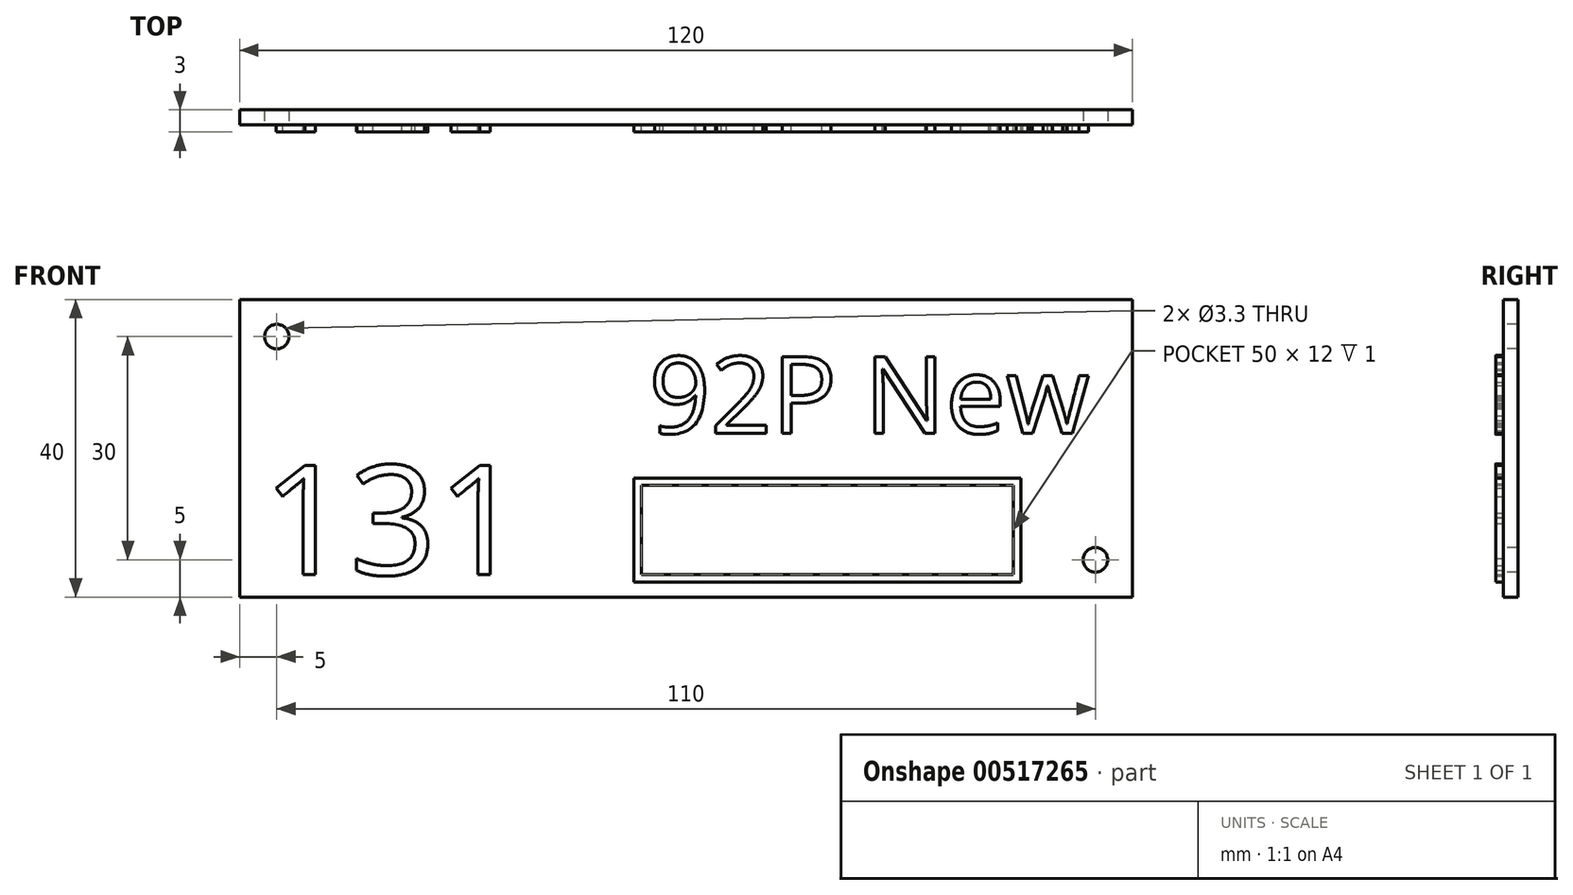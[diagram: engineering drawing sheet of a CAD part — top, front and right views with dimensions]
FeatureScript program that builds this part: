
annotation { "Feature Type Name" : "Feature", "Feature Type Description" : "" }
export const myFeature = defineFeature(function(context is Context, id is Id, definition is map)
    precondition{}
    {
        {
            var Q0;
            Q0=qCreatedBy(makeId("Front.planeOp"),FACE);
            var sketch = newSketch(context, id + "F0", { "sketchPlane" : qUnion([Q0])});
            skLineSegment(sketch, "E0.bottom", {"start": v(60, -20) * mm, "end": v(-60, -20) * mm});
            skLineSegment(sketch, "E0.top", {"start": v(60, 20) * mm, "end": v(-60, 20) * mm});
            skLineSegment(sketch, "E0.left", {"start": v(60, -20) * mm, "end": v(60, 20) * mm});
            skLineSegment(sketch, "E0.right", {"start": v(-60, -20) * mm, "end": v(-60, 20) * mm});
            skPoint(sketch, "E0.middle", {"position": v(0, 0) * mm});
            skSolve(sketch);
        }
        {
            var Q0;
            Q0=makeQuery(id+"F0.imprint","IMPRINT",FACE,{"disambiguationData":[TD([[makeQuery(id+"F0.imprint","IMPRINT",EDGE,{"derivedFrom":sQuery(id+"F0.wireOp",EDGE,"E0.bottom")}),-1.0]])]});
            extrude(context, id + "F1", {"entities" : qUnion([Q0]), "depth" : 2 * mm});
        }
        {
            var Q0;
            Q0=makeQuery(id+"F1.opExtrude","CAP_FACE",FACE,{"disambiguationData":[OSD([sQuery(id+"F0.wireOp",EDGE,"E0.bottom"),sQuery(id+"F0.wireOp",EDGE,"E0.top"),sQuery(id+"F0.wireOp",EDGE,"E0.left"),sQuery(id+"F0.wireOp",EDGE,"E0.right")])],"isStart":false});
            var sketch = newSketch(context, id + "F2", { "sketchPlane" : qUnion([Q0])});
            skPoint(sketch, "E1", {"position": v(-55, 15) * mm});
            skPoint(sketch, "E2", {"position": v(55, -15) * mm});
            skSolve(sketch);
        }
        {
            var Q0;
            Q0=sQuery(id+"F2.wireOp",VERTEX,"E1");
            var Q1;
            Q1=sQuery(id+"F2.wireOp",VERTEX,"E2");
            var Q2;
            Q2=makeQuery(id+"F1.opExtrude","SWEPT_BODY",BODY,{"disambiguationData":[OSD([sQuery(id+"F0.wireOp",EDGE,"E0.bottom"),sQuery(id+"F0.wireOp",EDGE,"E0.top"),sQuery(id+"F0.wireOp",EDGE,"E0.left"),sQuery(id+"F0.wireOp",EDGE,"E0.right")])]});
            hole(context, id + "F3", {"style" : HoleStyle.SIMPLE, "endStyle" : HoleEndStyle.THROUGH, "holeDiameter" : 3.3 * mm, "locations" : qUnion([Q0, Q1]), "scope" : qUnion([Q2]), "isTappedThrough" : true});
        }
        {
            var Q0;
            Q0=makeQuery(id+"F1.opExtrude","CAP_FACE",FACE,{"disambiguationData":[OSD([sQuery(id+"F0.wireOp",EDGE,"E0.bottom"),sQuery(id+"F0.wireOp",EDGE,"E0.top"),sQuery(id+"F0.wireOp",EDGE,"E0.left"),sQuery(id+"F0.wireOp",EDGE,"E0.right")])],"isStart":false});
            var sketch = newSketch(context, id + "F4", { "sketchPlane" : qUnion([Q0])});
            skText(sketch, "E3", { "text": "92P New", "fontName": "OpenSans-Regular.ttf"});
            const initialGuessF4  = {"E3": [-0.005, 0.002, 1, 0, 0.0104]};
            skSetInitialGuess(sketch, initialGuessF4);
            skSolve(sketch);
        }
        {
            var Q0;
            Q0=qSketchRegion(id+"F4",true);
            extrude(context, id + "F5", {"entities" : qUnion([Q0]), "operationType" : NewBodyOperationType.ADD, "depth" : 1 * mm});
        }
        {
            var Q0;
            {var subQ0=sQuery(id+"F0.wireOp",EDGE,"E0.top");var subQ1=sQuery(id+"F0.wireOp",EDGE,"E0.left");var subQ2=sQuery(id+"F0.wireOp",EDGE,"E0.right");var subQ3=sQuery(id+"F0.wireOp",EDGE,"E0.bottom");Q0=makeQuery(id+"F5.boolean.opBoolean","SPLIT",FACE,{"disambiguationData":[TD([makeQuery(id+"F1.opExtrude","SWEPT_FACE",FACE,{"disambiguationData":[OSD([subQ3])]})])],"derivedFrom":makeQuery(id+"F1.opExtrude","CAP_FACE",FACE,{"disambiguationData":[OSD([subQ3,subQ0,subQ1,subQ2])],"isStart":false})});}
            var sketch = newSketch(context, id + "F6", { "sketchPlane" : qUnion([Q0])});
            skText(sketch, "E4", { "text": "131", "fontName": "OpenSans-Regular.ttf"});
            const initialGuessF6  = {"E4": [-0.057, -0.017, 1, 0, 0.0148]};
            skSetInitialGuess(sketch, initialGuessF6);
            skSolve(sketch);
        }
        {
            var Q0;
            Q0=qSketchRegion(id+"F6",true);
            extrude(context, id + "F7", {"entities" : qUnion([Q0]), "operationType" : NewBodyOperationType.ADD, "depth" : 1 * mm});
        }
        {
            var Q0;
            {var subQ46=sQuery(id+"F0.wireOp",EDGE,"E0.top");var subQ48=sQuery(id+"F0.wireOp",EDGE,"E0.left");var subQ66=sQuery(id+"F0.wireOp",EDGE,"E0.right");var subQ76=sQuery(id+"F0.wireOp",EDGE,"E0.bottom");var subQ77=makeQuery(id+"F1.opExtrude","SWEPT_FACE",FACE,{"disambiguationData":[OSD([subQ76])]});Q0=makeQuery(id+"F7.boolean.opBoolean","SPLIT",FACE,{"disambiguationData":[TD([subQ77])],"derivedFrom":makeQuery(id+"F5.boolean.opBoolean","SPLIT",FACE,{"disambiguationData":[TD([subQ77])],"derivedFrom":makeQuery(id+"F1.opExtrude","CAP_FACE",FACE,{"disambiguationData":[OSD([subQ76,subQ46,subQ48,subQ66])],"isStart":false})})});}
            var sketch = newSketch(context, id + "F8", { "sketchPlane" : qUnion([Q0])});
            skLineSegment(sketch, "E5.bottom", {"start": v(45, -18) * mm, "end": v(-7, -18) * mm});
            skLineSegment(sketch, "E5.top", {"start": v(45, -4) * mm, "end": v(-7, -4) * mm});
            skLineSegment(sketch, "E5.left", {"start": v(45, -18) * mm, "end": v(45, -4) * mm});
            skLineSegment(sketch, "E5.right", {"start": v(-7, -18) * mm, "end": v(-7, -4) * mm});
            skPoint(sketch, "E5.middle", {"position": v(19, -11) * mm});
            skLineSegment(sketch, "E6.0", {"start": v(44, -5) * mm, "end": v(-6, -5) * mm});
            skLineSegment(sketch, "E6.1", {"start": v(44, -17) * mm, "end": v(44, -5) * mm});
            skLineSegment(sketch, "E6.2", {"start": v(44, -17) * mm, "end": v(-6, -17) * mm});
            skLineSegment(sketch, "E6.3", {"start": v(-6, -17) * mm, "end": v(-6, -5) * mm});
            skSolve(sketch);
        }
        {
            var Q0;
            Q0=makeQuery(id+"F8.imprint","IMPRINT",FACE,{"disambiguationData":[TD([[makeQuery(id+"F8.imprint","IMPRINT",EDGE,{"derivedFrom":sQuery(id+"F8.wireOp",EDGE,"E5.bottom")}),-1.0]])]});
            extrude(context, id + "F9", {"entities" : qUnion([Q0]), "operationType" : NewBodyOperationType.ADD, "depth" : 1 * mm});
        }
    });
